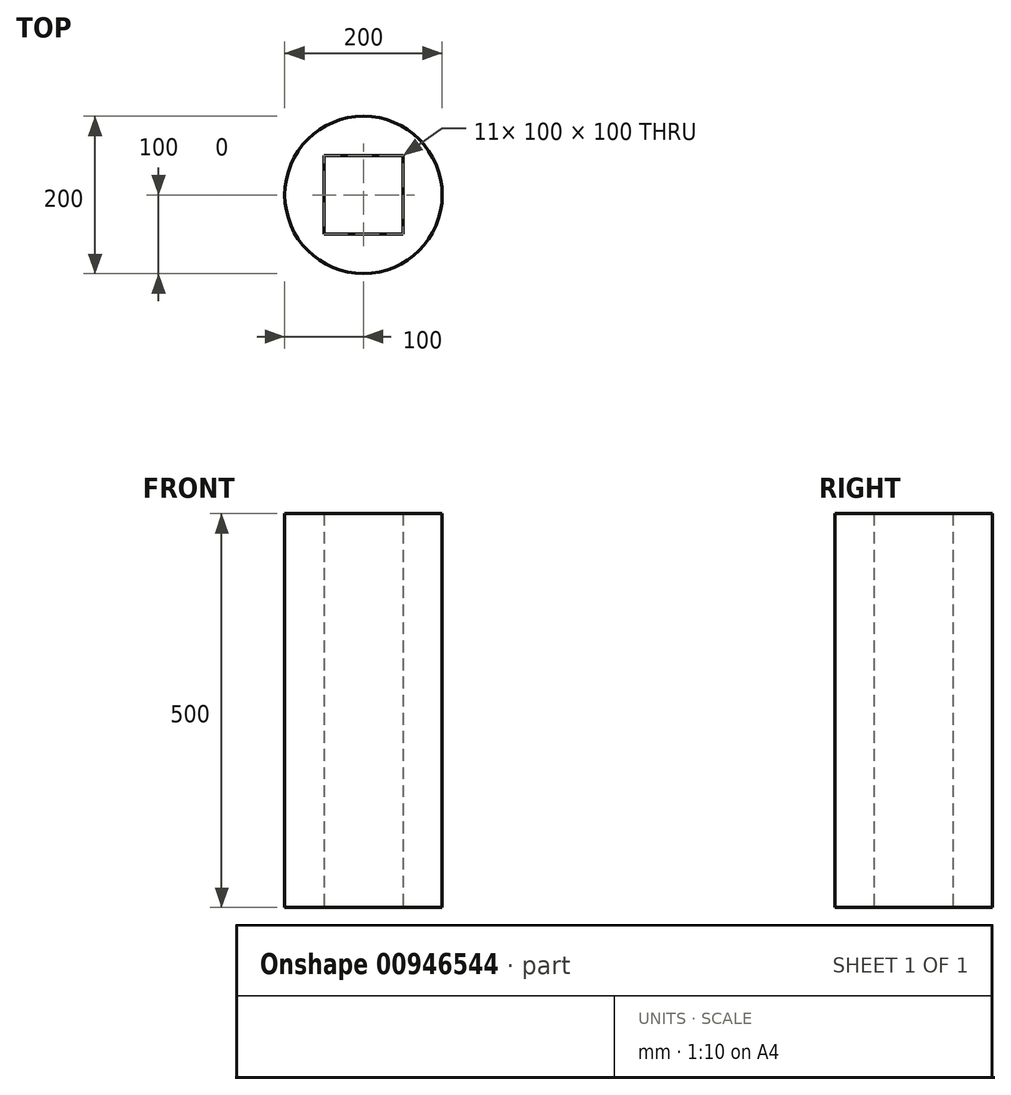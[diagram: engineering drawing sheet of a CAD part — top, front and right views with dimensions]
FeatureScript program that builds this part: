
annotation { "Feature Type Name" : "Feature", "Feature Type Description" : "" }
export const myFeature = defineFeature(function(context is Context, id is Id, definition is map)
    precondition{}
    {
        {
            var Q0;
            Q0=qCreatedBy(makeId("Top.planeOp"),FACE);
            var sketch = newSketch(context, id + "F0", { "sketchPlane" : qUnion([Q0])});
            skCircle(sketch, "E0", {"center": v(0, 0) * mm, "radius": 100 * mm});
            skLineSegment(sketch, "E1.bottom", {"start": v(50, -50) * mm, "end": v(-50, -50) * mm});
            skLineSegment(sketch, "E1.top", {"start": v(50, 50) * mm, "end": v(-50, 50) * mm});
            skLineSegment(sketch, "E1.left", {"start": v(50, -50) * mm, "end": v(50, 50) * mm});
            skLineSegment(sketch, "E1.right", {"start": v(-50, -50) * mm, "end": v(-50, 50) * mm});
            skSolve(sketch);
        }
        {
            var Q0;
            Q0 = qSketchRegion(id + "F0", true);
            extrude(context, id + "F1", {"entities" : qUnion([Q0]), "depth" : 500 * mm, "offsetDistance" : 25 * mm});
        }
    });
